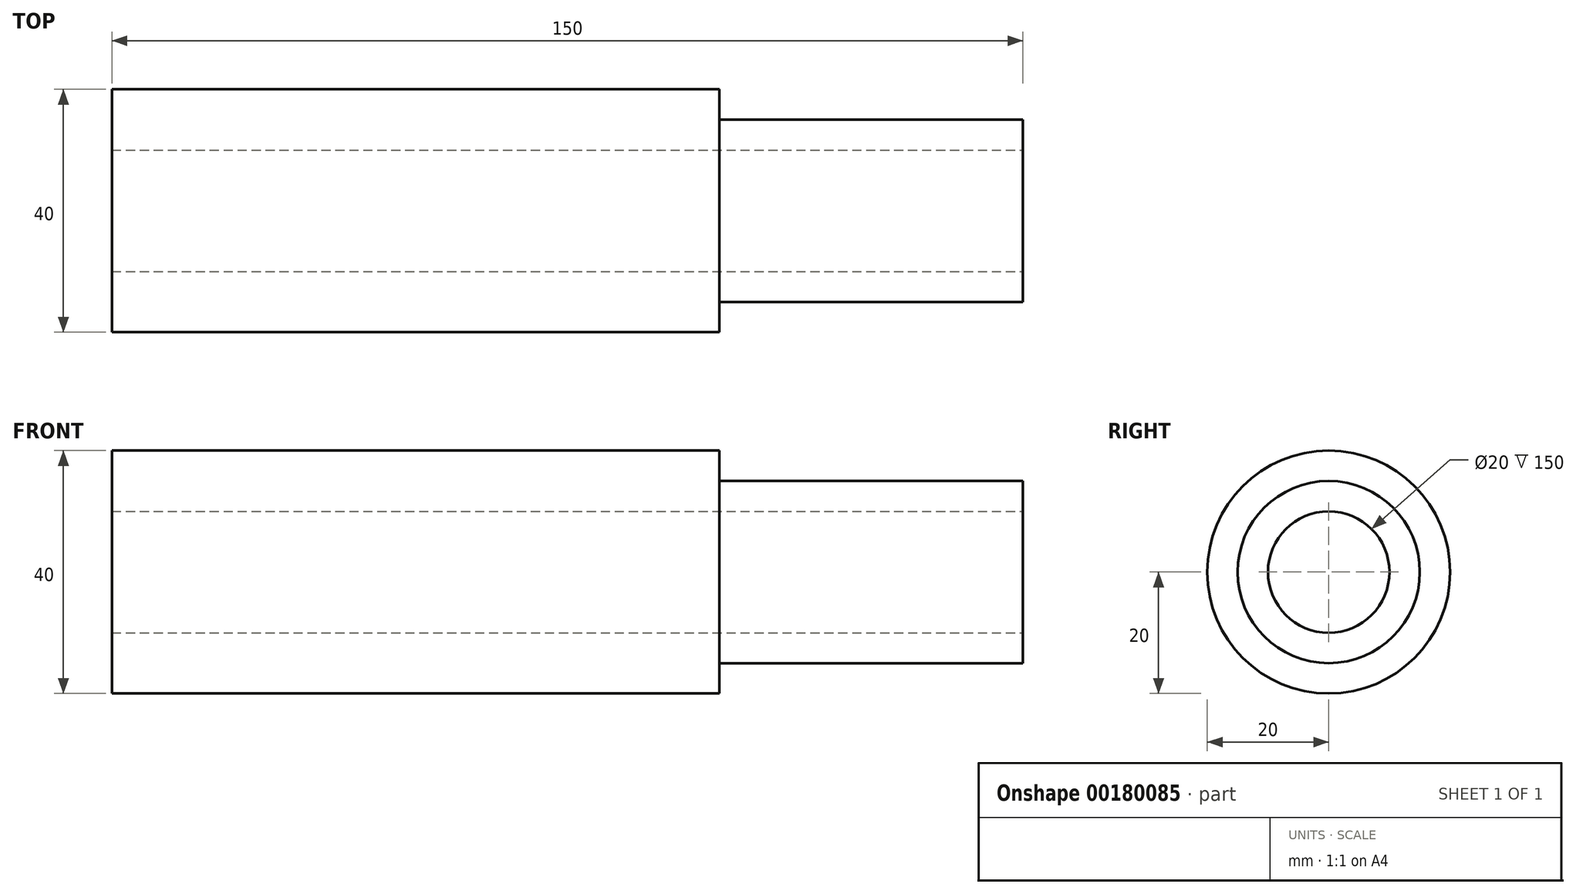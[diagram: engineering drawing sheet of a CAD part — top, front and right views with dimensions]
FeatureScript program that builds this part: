
annotation { "Feature Type Name" : "Feature", "Feature Type Description" : "" }
export const myFeature = defineFeature(function(context is Context, id is Id, definition is map)
    precondition{}
    {
        {
            var Q0;
            Q0=qCreatedBy(makeId("Right.planeOp"),FACE);
            var sketch = newSketch(context, id + "F0", { "sketchPlane" : qUnion([Q0])});
            skCircle(sketch, "E0", {"center": v(0, 0) * mm, "radius": 20 * mm});
            skCircle(sketch, "E1", {"center": v(0, 0) * mm, "radius": 10 * mm});
            skSolve(sketch);
        }
        {
            var Q0;
            Q0=makeQuery(id+"F0.imprint","IMPRINT",FACE,{"disambiguationData":[TD([[makeQuery(id+"F0.imprint","IMPRINT",EDGE,{"derivedFrom":sQuery(id+"F0.wireOp",EDGE,"E0")}),1.0]])]});
            extrude(context, id + "F1", {"entities" : qUnion([Q0]), "oppositeDirection" : true, "depth" : 150 * mm});
        }
        {
            var Q0;
            Q0=makeQuery(id+"F1.opExtrude","CAP_FACE",FACE,{"disambiguationData":[OSD([sQuery(id+"F0.wireOp",EDGE,"E0"),sQuery(id+"F0.wireOp",EDGE,"E1")])],"isStart":true});
            var sketch = newSketch(context, id + "F2", { "sketchPlane" : qUnion([Q0])});
            skCircle(sketch, "E2", {"center": v(0, 0) * mm, "radius": 15 * mm});
            skSolve(sketch);
        }
        {
            var Q0;
            Q0=makeQuery(id+"F2.imprint","IMPRINT",FACE,{"disambiguationData":[TD([[makeQuery(id+"F2.imprint","IMPRINT",EDGE,{"derivedFrom":sQuery(id+"F2.wireOp",EDGE,"E2")}),-1.0]])]});
            extrude(context, id + "F3", {"entities" : qUnion([Q0]), "operationType" : NewBodyOperationType.REMOVE, "oppositeDirection" : true, "depth" : 50 * mm});
        }
    });
